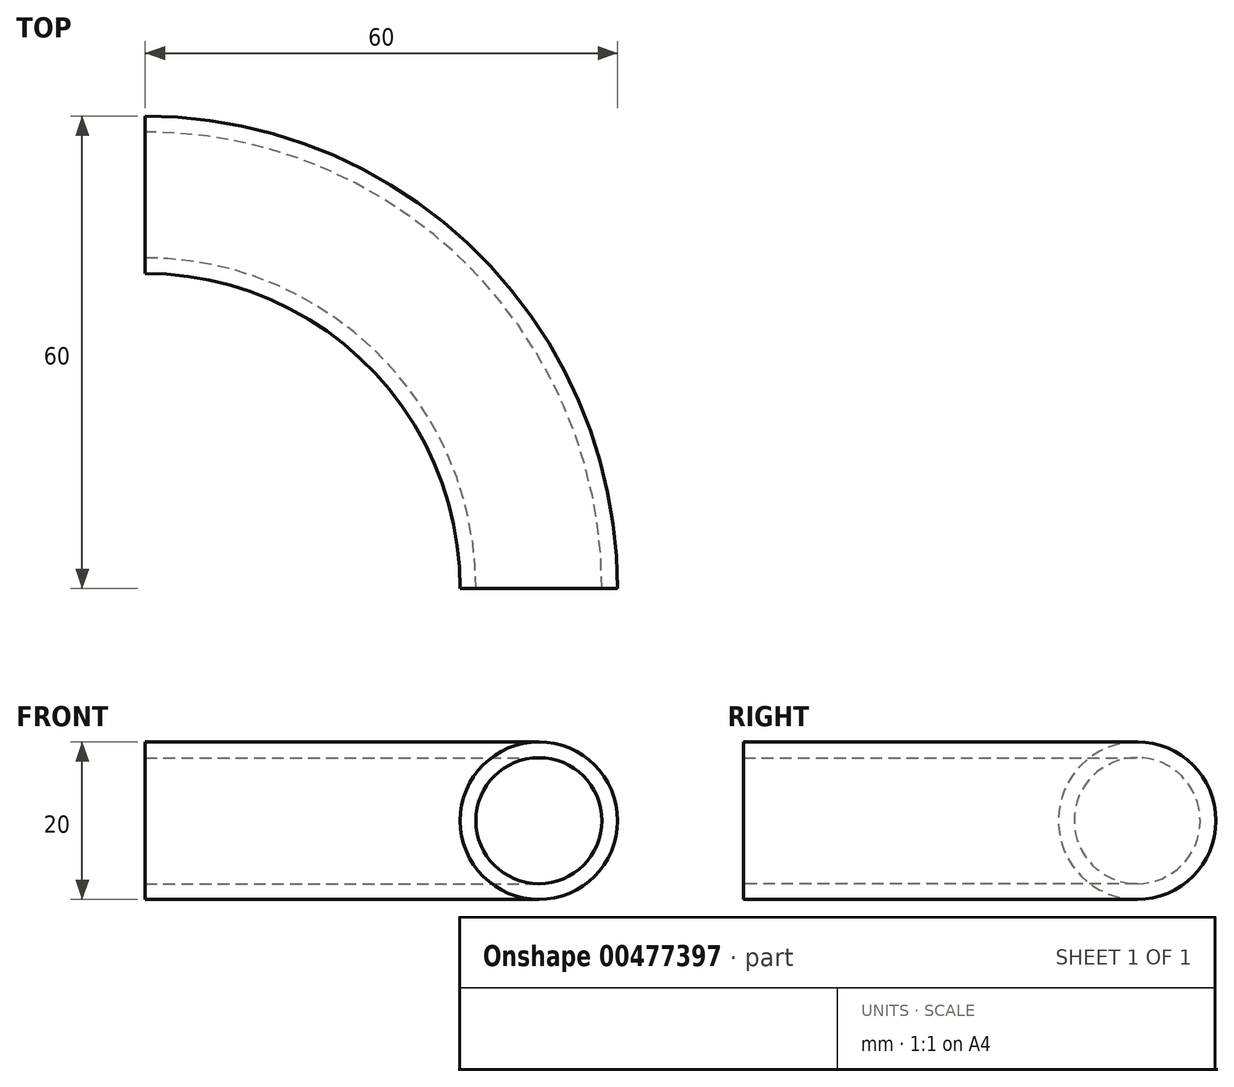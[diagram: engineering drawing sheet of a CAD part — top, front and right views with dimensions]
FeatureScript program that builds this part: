
annotation { "Feature Type Name" : "Feature", "Feature Type Description" : "" }
export const myFeature = defineFeature(function(context is Context, id is Id, definition is map)
    precondition{}
    {
        {
            var Q0;
            Q0=qCreatedBy(makeId("Top.planeOp"),FACE);
            var sketch = newSketch(context, id + "F0", { "sketchPlane" : qUnion([Q0])});
            skArc(sketch, "E0", {"start": v(50, 0) * mm, "mid": v(35.36, 35.36) * mm, "end": v(0, 50) * mm});
            skSolve(sketch);
        }
        {
            var Q0;
            Q0=qCreatedBy(makeId("Right.planeOp"),FACE);
            var sketch = newSketch(context, id + "F1", { "sketchPlane" : qUnion([Q0])});
            skCircle(sketch, "E1", {"center": v(50, 0) * mm, "radius": 10 * mm});
            skCircle(sketch, "E2", {"center": v(50, 0) * mm, "radius": 8 * mm});
            skSolve(sketch);
        }
        {
            var Q0;
            Q0=makeQuery(id+"F1.imprint","IMPRINT",FACE,{"disambiguationData":[TD([[makeQuery(id+"F1.imprint","IMPRINT",EDGE,{"derivedFrom":sQuery(id+"F1.wireOp",EDGE,"E1")}),1.0]])]});
            var Q1;
            Q1=sQuery(id+"F0.wireOp",EDGE,"E0");
            sweep(context, id + "F2", {"profiles" : qUnion([Q0]), "path" : qUnion([Q1])});
        }
    });
